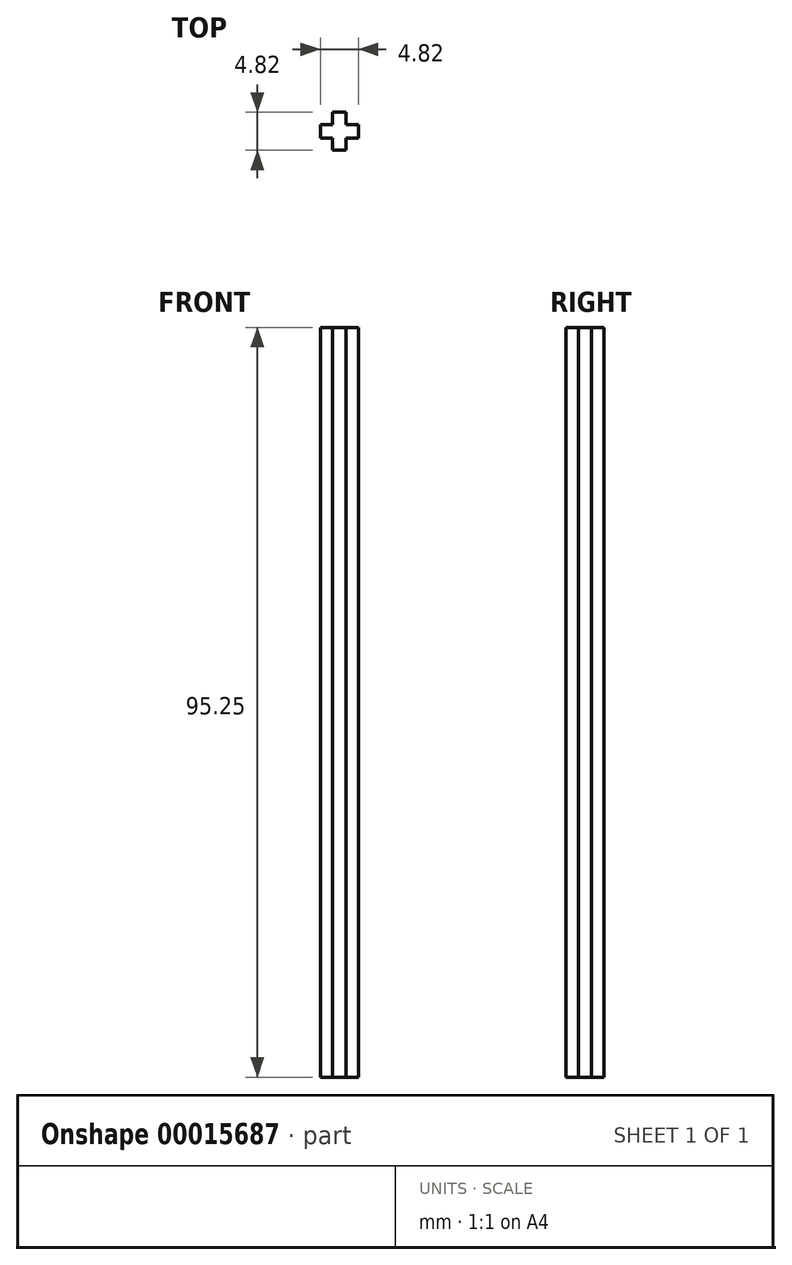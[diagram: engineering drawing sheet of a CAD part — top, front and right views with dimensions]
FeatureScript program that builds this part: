
annotation { "Feature Type Name" : "Feature", "Feature Type Description" : "" }
export const myFeature = defineFeature(function(context is Context, id is Id, definition is map)
    precondition{}
    {
        {
            var Q0;
            Q0=qCreatedBy(makeId("Top.planeOp"),FACE);
            var sketch = newSketch(context, id + "F0", { "sketchPlane" : qUnion([Q0])});
            skLineSegment(sketch, "E0.rect.bottom", {"start": v(2.41, -0.84) * mm, "end": v(-2.41, -0.84) * mm});
            skLineSegment(sketch, "E0.rect.top", {"start": v(2.41, 0.84) * mm, "end": v(-2.41, 0.84) * mm});
            skLineSegment(sketch, "E0.rect.left", {"start": v(2.41, -0.84) * mm, "end": v(2.41, 0.84) * mm});
            skLineSegment(sketch, "E0.rect.right", {"start": v(-2.41, -0.84) * mm, "end": v(-2.41, 0.84) * mm});
            skPoint(sketch, "E0.rect.middle", {"position": v(0, 0) * mm});
            skLineSegment(sketch, "E1.rect.bottom", {"start": v(0.84, -2.41) * mm, "end": v(-0.84, -2.41) * mm});
            skLineSegment(sketch, "E1.rect.top", {"start": v(0.84, 2.41) * mm, "end": v(-0.84, 2.41) * mm});
            skLineSegment(sketch, "E1.rect.left", {"start": v(0.84, -2.41) * mm, "end": v(0.84, 2.41) * mm});
            skLineSegment(sketch, "E1.rect.right", {"start": v(-0.84, -2.41) * mm, "end": v(-0.84, 2.41) * mm});
            skSolve(sketch);
        }
        {
            var Q0;
            Q0 = qSketchRegion(id + "F0", true);
            extrude(context, id + "F1", {"entities" : qUnion([Q0]), "depth" : 95.25 * mm});
        }
    });
